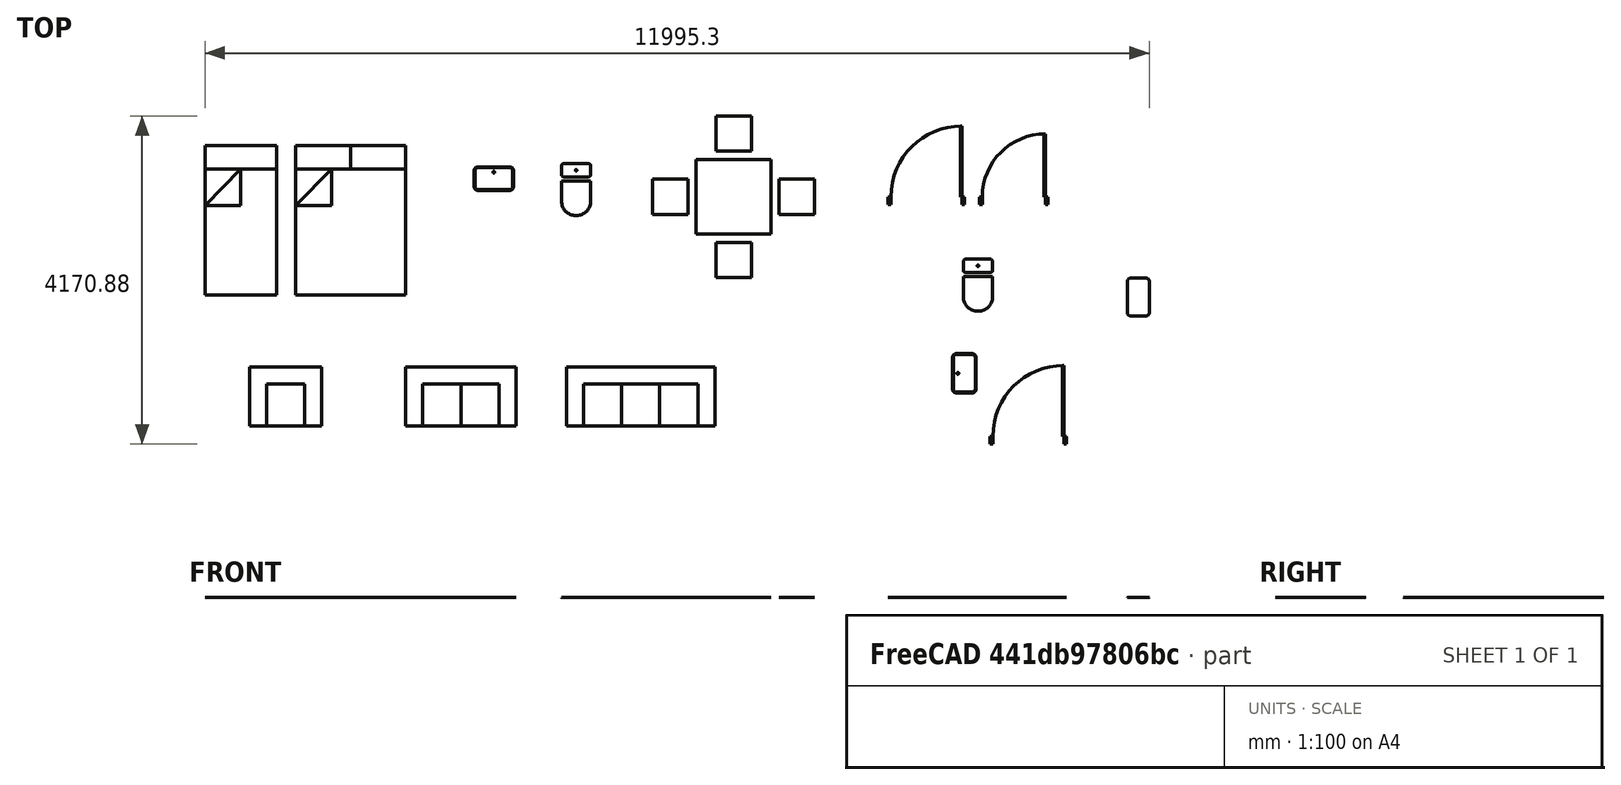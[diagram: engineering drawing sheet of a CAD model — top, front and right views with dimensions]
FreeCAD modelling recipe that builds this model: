
FCSTD DOCUMENT  (FreeCAD 0.17R10168 (Git))
Label: 2D Assets 02
License: All rights reserved
LicenseURL: http://en.wikipedia.org/wiki/All_rights_reserved
objects: Part::Part2DObjectPython×45, Part::Feature×9, Part::Compound×8, App::DocumentObjectGroup×3, App::FeaturePython×2
note: 62 computed .brp shape members not serialized (recipe doc carries the construction recipe); baked Part::Feature solids carry a one-line shape summary decoded from their .brp

FEATURE [Part::Feature] Shell  label="Dinning "
  shape: bbox 2057 x 2057 x 2e-07 mm, 5 faces, 0 solids (baked)
FEATURE [Part::Part2DObjectPython] Rectangle009  # Draft 2D object (typed FeaturePython)
  ChamferSize = 0
  Columns = 1
  FilletRadius = 0
  Height = 18
  Length = 900
  MakeFace = true
  Placement = pos=(3354.54,473.858,0) rot=(0.707107,0.707107,0;3.14159rad)
  Rows = 1
FEATURE [Part::Part2DObjectPython] Arc  # Draft 2D object (typed FeaturePython)
  FirstAngle = -90
  LastAngle = 0
  MakeFace = true
  Placement = pos=(3372.54,473.858,0) rot=(0.707107,0.707107,0;3.14159rad)
  Radius = 900
FEATURE [Part::Part2DObjectPython] Rectangle006  # Draft 2D object (typed FeaturePython)
  ChamferSize = 0
  Columns = 1
  FilletRadius = 0
  Height = 18
  Length = 100
  MakeFace = true
  Placement = pos=(3390.54,373.858,0) rot=(0.707107,0.707107,0;3.14159rad)
  Rows = 1
FEATURE [Part::Part2DObjectPython] Rectangle005  # Draft 2D object (typed FeaturePython)
  ChamferSize = 0
  Columns = 1
  FilletRadius = 0
  Height = 18
  Length = 100
  MakeFace = true
  Placement = pos=(3372.54,373.858,0) rot=(0.707107,0.707107,0;3.14159rad)
  Rows = 1
FEATURE [Part::Part2DObjectPython] Rectangle004  # Draft 2D object (typed FeaturePython)
  ChamferSize = 0
  Columns = 1
  FilletRadius = 0
  Height = 18
  Length = 100
  MakeFace = true
  Placement = pos=(2436.54,373.858,0) rot=(0.707107,0.707107,0;3.14159rad)
  Rows = 1
FEATURE [Part::Part2DObjectPython] Rectangle002  # Draft 2D object (typed FeaturePython)
  ChamferSize = 0
  Columns = 1
  FilletRadius = 0
  Height = 18
  Length = 100
  MakeFace = true
  Placement = pos=(2454.54,373.858,0) rot=(0.707107,0.707107,0;3.14159rad)
  Rows = 1
FEATURE [Part::Compound] Compound  label="Door-90cm"
  Links = -> [Rectangle002,Rectangle004,Rectangle009,Rectangle006,Arc,Rectangle005]
  Placement = pos=(0,-3.0421,0) rot=(0,0,1;0rad)
FEATURE [Part::Part2DObjectPython] Rectangle  # Draft 2D object (typed FeaturePython)
  ChamferSize = 0
  Columns = 1
  FilletRadius = 0
  Height = 1450
  Length = 2250
  MakeFace = false
  Placement = pos=(3253.57,-2571.26,0) rot=(0.707107,0.707107,0;3.14159rad)
  Rows = 1
FEATURE [Part::Part2DObjectPython] Rectangle010  # Draft 2D object (typed FeaturePython)
  ChamferSize = 0
  Columns = 1
  FilletRadius = 0
  Height = 18
  Length = 800
  MakeFace = true
  Placement = pos=(4414.52,473.858,0) rot=(0.707107,0.707107,0;3.14159rad)
  Rows = 1
FEATURE [Part::Part2DObjectPython] Rectangle011  # Draft 2D object (typed FeaturePython)
  ChamferSize = 0
  Columns = 1
  FilletRadius = 0
  Height = 18
  Length = 100
  MakeFace = true
  Placement = pos=(4450.52,373.858,0) rot=(0.707107,0.707107,0;3.14159rad)
  Rows = 1
FEATURE [Part::Part2DObjectPython] Rectangle012  # Draft 2D object (typed FeaturePython)
  ChamferSize = 0
  Columns = 1
  FilletRadius = 0
  Height = 18
  Length = 100
  MakeFace = true
  Placement = pos=(4432.52,373.858,0) rot=(0.707107,0.707107,0;3.14159rad)
  Rows = 1
FEATURE [Part::Part2DObjectPython] Rectangle013  # Draft 2D object (typed FeaturePython)
  ChamferSize = 0
  Columns = 1
  FilletRadius = 0
  Height = 18
  Length = 100
  MakeFace = true
  Placement = pos=(3596.52,373.858,0) rot=(0.707107,0.707107,0;3.14159rad)
  Rows = 1
FEATURE [Part::Part2DObjectPython] Rectangle014  # Draft 2D object (typed FeaturePython)
  ChamferSize = 0
  Columns = 1
  FilletRadius = 0
  Height = 18
  Length = 100
  MakeFace = true
  Placement = pos=(3614.52,373.858,0) rot=(0.707107,0.707107,0;3.14159rad)
  Rows = 1
FEATURE [Part::Feature] Clone002  label="Clone of Door-90cm002"
  Placement = pos=(1295.04,-3045.12,0) rot=(0,0,1;0rad)
  shape: bbox 972 x 1000 x 2e-07 mm, 5 faces, 0 solids (baked)
FEATURE [Part::Part2DObjectPython] Rectangle015  # Draft 2D object (typed FeaturePython)
  ChamferSize = 0
  Columns = 1
  FilletRadius = 0
  Height = 1655.27
  Length = 2455.27
  MakeFace = false
  Placement = pos=(3150.94,-2673.89,0) rot=(0.707107,0.707107,0;3.14159rad)
  Rows = 1
FEATURE [Part::Part2DObjectPython] Rectangle016  # Draft 2D object (typed FeaturePython)
  ChamferSize = 0
  Columns = 1
  FilletRadius = 0
  Height = 800
  Length = 800
  MakeFace = true
  Placement = pos=(5424.98,155.631,0) rot=(0.707107,0.707107,0;3.14159rad)
  Rows = 1
FEATURE [Part::Part2DObjectPython] Rectangle017  # Draft 2D object (typed FeaturePython)
  ChamferSize = 0
  Columns = 1
  FilletRadius = 0
  Height = 760
  Length = 760
  MakeFace = true
  Placement = pos=(5444.98,175.631,0) rot=(0.707107,0.707107,0;3.14159rad)
  Rows = 1
FEATURE [Part::Feature] Face
  shape: bbox 800 x 800 x 2e-07 mm, 1 faces, 0 solids (baked)
FEATURE [Part::Part2DObjectPython] Rectangle018  # Draft 2D object (typed FeaturePython)
  ChamferSize = 0
  Columns = 1
  FilletRadius = 0
  Height = 760
  Length = 760
  MakeFace = true
  Placement = pos=(5444.98,175.631,0) rot=(0.707107,0.707107,0;3.14159rad)
  Rows = 1
FEATURE [Part::Part2DObjectPython] Line001  # Draft 2D object (typed FeaturePython)
  ChamferSize = 0
  Closed = false
  End = (5444.98,175.631,0)
  FilletRadius = 0
  Length = 1074.8
  MakeFace = true
  Points = (2) [(6204.98,935.631,0),(5444.98,175.631,0)]
  Start = (6204.98,935.631,0)
  Subdivisions = 0
FEATURE [Part::Part2DObjectPython] Line002  # Draft 2D object (typed FeaturePython)
  ChamferSize = 0
  Closed = false
  End = (6204.98,175.631,0)
  FilletRadius = 0
  Length = 1074.8
  MakeFace = true
  Points = (2) [(5444.98,935.631,0),(6204.98,175.631,0)]
  Start = (5444.98,935.631,0)
  Subdivisions = 0
FEATURE [Part::Part2DObjectPython] Block  label="Shower"  # Draft 2D object (typed FeaturePython)
  Components = -> [Line002,Line001,Rectangle018,Face]
  Placement = pos=(-1521.4,-1276.89,0) rot=(0,0,1;0rad)
FEATURE [Part::Part2DObjectPython] Rectangle020  # Draft 2D object (typed FeaturePython)
  ChamferSize = 0
  Columns = 1
  FilletRadius = 30
  Height = 370
  Length = 170
  MakeFace = true
  Placement = pos=(6394.93,-418.973,0) rot=(0.707107,0.707107,0;3.14159rad)
  Rows = 1
FEATURE [Part::Part2DObjectPython] Circle  # Draft 2D object (typed FeaturePython)
  FirstAngle = 0
  LastAngle = 0
  MakeFace = true
  Placement = pos=(6579.93,-333.973,0) rot=(0.707107,0.707107,0;3.14159rad)
  Radius = 10
  Support = -> [Rectangle020]
FEATURE [Part::Feature] Compound003  label="WC001"
  Placement = pos=(-3002.47,-72.2332,0) rot=(0,0,1;0rad)
  shape: bbox 370 x 660 x 2e-07 mm, 2 faces, 0 solids (baked)
FEATURE [Part::Part2DObjectPython] Rectangle021  # Draft 2D object (typed FeaturePython)
  ChamferSize = 0
  Columns = 1
  FilletRadius = 50
  Height = 300
  Length = 500
  MakeFace = true
  Placement = pos=(5464.52,-1052.21,0) rot=(0.707107,0.707107,0;3.14159rad)
  Rows = 1
FEATURE [Part::Part2DObjectPython] Circle001  # Draft 2D object (typed FeaturePython)
  FirstAngle = 0
  LastAngle = 0
  MakeFace = true
  Placement = pos=(5532.19,-802.214,0) rot=(0,0,1;0rad)
  Radius = 12
FEATURE [Part::Feature] Face003
  shape: bbox 278.9 x 478.9 x 2e-07 mm, 1 faces, 0 solids (baked)
FEATURE [Part::Feature] Face004
  shape: bbox 278.9 x 478.9 x 2e-07 mm, 1 faces, 0 solids (baked)
FEATURE [Part::Feature] Face005
  shape: bbox 300 x 500 x 2e-07 mm, 1 faces, 0 solids (baked)
FEATURE [Part::Compound] Compound004  label="Sink 1"
  Links = -> [Face005,Face003,Circle001]
  Placement = pos=(-2210.95,-969.046,0) rot=(0,0,1;0rad)
FEATURE [Part::Feature] Compound005  label="Sink"
  Placement = pos=(-1770.47,6315.78,0) rot=(0,0,-1;1.5708rad)
  shape: bbox 500 x 300 x 2e-07 mm, 3 faces, 0 solids (baked)
FEATURE [Part::Feature] Compound006  label="WC002"
  Placement = pos=(-8107.39,1143,0) rot=(0,0,1;0rad)
  shape: bbox 370 x 660 x 2e-07 mm, 2 faces, 0 solids (baked)
FEATURE [Part::Part2DObjectPython] Arc002  # Draft 2D object (typed FeaturePython)
  FirstAngle = -90
  LastAngle = 0
  MakeFace = true
  Placement = pos=(4432.52,473.858,0) rot=(0.707107,0.707107,0;3.14159rad)
  Radius = 800
FEATURE [Part::Compound] Compound007  label="Door-80cm"
  Links = -> [Rectangle012,Rectangle010,Rectangle011,Rectangle013,Rectangle014,Arc002]
  Placement = pos=(0,-3.0421,0) rot=(0,0,1;0rad)
FEATURE [Part::Part2DObjectPython] Rectangle022  # Draft 2D object (typed FeaturePython)
  ChamferSize = 0
  Columns = 1
  FilletRadius = 0
  Height = 400
  Length = 400
  MakeFace = false
  Placement = pos=(-1527.46,494.024,0) rot=(0.707107,0.707107,0;3.14159rad)
  Rows = 1
FEATURE [Part::Part2DObjectPython] Rectangle023  # Draft 2D object (typed FeaturePython)
  ChamferSize = 0
  Columns = 1
  FilletRadius = 0
  Height = 400
  Length = 400
  MakeFace = false
  Placement = pos=(-1927.46,494.024,0) rot=(0.707107,0.707107,0;3.14159rad)
  Rows = 1
FEATURE [App::FeaturePython] Dimension  # Draft dimension (typed FeaturePython)
  Diameter = false
  Dimline = (-1142.39,1006.82,0)
  Direction = (0,0,0)
  Distance = 400
  End = (-1127.46,894.024,0)
  Normal = (0,0,1)
  Start = (-1527.46,894.024,0)
FEATURE [App::FeaturePython] Dimension001  # Draft dimension (typed FeaturePython)
  Diameter = false
  Dimline = (-1150.68,1079.22,0)
  Direction = (0,0,0)
  Distance = 800
  End = (-1127.46,894.024,0)
  Normal = (0,0,1)
  Start = (-1927.46,894.024,0)
FEATURE [App::DocumentObjectGroup] Construction
FEATURE [Part::Part2DObjectPython] Rectangle025  # Draft 2D object (typed FeaturePython)
  ChamferSize = 0
  Columns = 1
  FilletRadius = 0
  Height = 1900
  Length = 1400
  MakeFace = true
  Placement = pos=(-5091.08,-778.605,0) rot=(0,0,1;0rad)
  Rows = 1
FEATURE [Part::Part2DObjectPython] Rectangle027  # Draft 2D object (typed FeaturePython)
  ChamferSize = 0
  Columns = 1
  FilletRadius = 0
  Height = 1900
  Length = 910
  MakeFace = true
  Placement = pos=(-6241.3,-778.605,0) rot=(0,0,1;0rad)
  Rows = 1
FEATURE [Part::Part2DObjectPython] Rectangle029  # Draft 2D object (typed FeaturePython)
  ChamferSize = 0
  Columns = 1
  FilletRadius = 0
  Height = 300
  Length = 910
  MakeFace = true
  Placement = pos=(-6241.3,821.395,0) rot=(0,0,1;0rad)
  Rows = 1
FEATURE [Part::Part2DObjectPython] Line003  # Draft 2D object (typed FeaturePython)
  ChamferSize = 0
  Closed = false
  End = (-5786.3,821.395,0)
  FilletRadius = 0
  Length = 647.012
  MakeFace = true
  Points = (2) [(-6241.3,361.395,0),(-5786.3,821.395,0)]
  Start = (-6241.3,361.395,0)
  Subdivisions = 0
FEATURE [Part::Part2DObjectPython] DWire  # Draft 2D object (typed FeaturePython)
  ChamferSize = 0
  Closed = true
  End = (-6241.3,361.395,0)
  FilletRadius = 0
  Length = 1562.01
  MakeFace = true
  Points = (3) [(-5786.3,821.395,0),(-5786.3,361.395,0),(-6241.3,361.395,0)]
  Start = (-5786.3,821.395,0)
  Subdivisions = 0
FEATURE [Part::Part2DObjectPython] DWire001  # Draft 2D object (typed FeaturePython)
  ChamferSize = 0
  Closed = true
  End = (-5091.08,361.395,0)
  FilletRadius = 0
  Length = 1562.01
  MakeFace = true
  Placement = pos=(1150.22,0,0) rot=(0,0,1;0rad)
  Points = (3) [(-5786.3,821.395,0),(-5786.3,361.395,0),(-6241.3,361.395,0)]
  Start = (-4636.08,821.395,0)
  Subdivisions = 0
FEATURE [Part::Part2DObjectPython] Rectangle032  # Draft 2D object (typed FeaturePython)
  ChamferSize = 0
  Columns = 1
  FilletRadius = 0
  Height = 300
  Length = 700
  MakeFace = true
  Placement = pos=(-5091.08,821.395,0) rot=(0,0,1;0rad)
  Rows = 1
FEATURE [Part::Part2DObjectPython] Rectangle033  # Draft 2D object (typed FeaturePython)
  ChamferSize = 0
  Columns = 1
  FilletRadius = 0
  Height = 300
  Length = 700
  MakeFace = true
  Placement = pos=(-4391.08,821.395,0) rot=(0,0,1;0rad)
  Rows = 1
FEATURE [Part::Compound] Compound008  label="Bed-Double"
  Links = -> [Rectangle025,DWire001,Rectangle032,Rectangle033]
FEATURE [Part::Compound] Compound009  label="Bed-Twin"
  Links = -> [Rectangle027,Rectangle029,Line003,DWire]
FEATURE [App::DocumentObjectGroup] Group  label="Assets"
  Group = -> [Compound005,Compound006,Shell,Compound,Compound007,Compound008,Compound009,Dimension001,Rectangle022,Rectangle023,Dimension]
FEATURE [App::DocumentObjectGroup] Group001
  Group = -> [Rectangle,Clone002,Rectangle015,Rectangle016,Rectangle017,Face,Rectangle018,Line001,Line002,Block,Rectangle020,Circle,Compound003,Rectangle021,Face004,Compound004]
FEATURE [Part::Part2DObjectPython] DWire002  # Draft 2D object (typed FeaturePython)
  ChamferSize = 0
  Closed = true
  End = (-3474.44,-2441.09,0)
  FilletRadius = 0
  Length = 5366.71
  MakeFace = true
  Points = (8) [(-3691.08,-2441.09,0),(-3691.08,-1691.09,0),(-2291.08,-1691.09,0),(-2291.08,-2441.09,0),(-2507.72,-2441.09,0),(-2507.72,-1907.73,0),(-3474.44,-1907.73,0),(-3474.44,-2441.09,0)]
  Start = (-3691.08,-2441.09,0)
  Subdivisions = 0
FEATURE [Part::Part2DObjectPython] Rectangle035  # Draft 2D object (typed FeaturePython)
  ChamferSize = 0
  Columns = 1
  FilletRadius = 0
  Height = 533.356
  Length = 966.713
  MakeFace = true
  Placement = pos=(-3474.44,-2441.09,0) rot=(0,0,1;0rad)
  Rows = 1
FEATURE [Part::Part2DObjectPython] Line  # Draft 2D object (typed FeaturePython)
  ChamferSize = 0
  Closed = false
  End = (-2991.08,-2441.09,0)
  FilletRadius = 0
  Length = 533.356
  MakeFace = true
  Points = (2) [(-2991.08,-1907.73,0),(-2991.08,-2441.09,0)]
  Start = (-2991.08,-1907.73,0)
  Subdivisions = 0
FEATURE [Part::Part2DObjectPython] Line004  # Draft 2D object (typed FeaturePython)
  ChamferSize = 0
  Closed = false
  End = (-947.957,-2441.09,0)
  FilletRadius = 0
  Length = 533.356
  MakeFace = true
  Placement = pos=(2043.12,0,0) rot=(0,0,1;0rad)
  Points = (2) [(-2991.08,-1907.73,0),(-2991.08,-2441.09,0)]
  Start = (-947.957,-1907.73,0)
  Subdivisions = 0
FEATURE [Part::Part2DObjectPython] Rectangle036  # Draft 2D object (typed FeaturePython)
  ChamferSize = 0
  Columns = 1
  FilletRadius = 0
  Height = 533.356
  Length = 966.713
  MakeFace = true
  Placement = pos=(-1431.31,-2441.09,0) rot=(0,0,1;0rad)
  Rows = 1
FEATURE [Part::Part2DObjectPython] DWire003  # Draft 2D object (typed FeaturePython)
  ChamferSize = 0
  Closed = true
  End = (-1431.31,-2441.09,0)
  FilletRadius = 0
  Length = 6333.43
  MakeFace = true
  Placement = pos=(2043.12,0,0) rot=(0,0,1;0rad)
  Points = (8) [(-3691.08,-2441.09,0),(-3691.08,-1691.09,0),(-1807.72,-1691.09,0),(-1807.72,-2441.09,0),(-2024.37,-2441.09,0),(-2024.37,-1907.73,0),(-3474.44,-1907.73,0),(-3474.44,-2441.09,0)]
  Start = (-1647.96,-2441.09,0)
  Subdivisions = 0
FEATURE [Part::Part2DObjectPython] Line005  # Draft 2D object (typed FeaturePython)
  ChamferSize = 0
  Closed = false
  End = (-4974.49,-2441.09,0)
  FilletRadius = 0
  Length = 533.356
  MakeFace = true
  Placement = pos=(-1983.42,0,0) rot=(0,0,1;0rad)
  Points = (2) [(-2991.08,-1907.73,0),(-2991.08,-2441.09,0)]
  Start = (-4974.49,-1907.73,0)
  Subdivisions = 0
FEATURE [Part::Part2DObjectPython] DWire004  # Draft 2D object (typed FeaturePython)
  ChamferSize = 0
  Closed = true
  End = (-5457.85,-2441.09,0)
  FilletRadius = 0
  Length = 4400
  MakeFace = true
  Placement = pos=(-1983.42,0,0) rot=(0,0,1;0rad)
  Points = (8) [(-3691.08,-2441.09,0),(-3691.08,-1691.09,0),(-2774.44,-1691.09,0),(-2774.44,-2441.09,0),(-2991.08,-2441.09,0),(-2991.08,-1907.73,0),(-3474.44,-1907.73,0),(-3474.44,-2441.09,0)]
  Start = (-5674.49,-2441.09,0)
  Subdivisions = 0
FEATURE [Part::Part2DObjectPython] Rectangle037  # Draft 2D object (typed FeaturePython)
  ChamferSize = 0
  Columns = 1
  FilletRadius = 0
  Height = 533.356
  Length = 483.356
  MakeFace = true
  Placement = pos=(-5457.85,-2441.09,0) rot=(0,0,1;0rad)
  Rows = 1
FEATURE [Part::Compound] Compound010  label="Sofa - 1"
  Links = -> [DWire002,Rectangle035,Line]
FEATURE [Part::Compound] Compound011  label="Sofa - 2"
  Links = -> [Rectangle037,DWire004]
FEATURE [Part::Part2DObjectPython] Rectangle038  # Draft 2D object (typed FeaturePython)
  ChamferSize = 0
  Columns = 1
  FilletRadius = 0
  Height = 533.356
  Length = 1450.07
  MakeFace = true
  Placement = pos=(-1431.31,-2441.09,0) rot=(0,0,1;0rad)
  Rows = 1
FEATURE [Part::Part2DObjectPython] Line006  # Draft 2D object (typed FeaturePython)
  ChamferSize = 0
  Closed = false
  End = (-464.6,-2441.09,0)
  FilletRadius = 0
  Length = 533.356
  MakeFace = true
  Placement = pos=(2526.48,0,0) rot=(0,0,1;0rad)
  Points = (2) [(-2991.08,-1907.73,0),(-2991.08,-2441.09,0)]
  Start = (-464.6,-1907.73,0)
  Subdivisions = 0
FEATURE [Part::Compound] Compound012  label="Sofa - 3"
  Links = -> [Line004,DWire003,Rectangle038,Line006]
